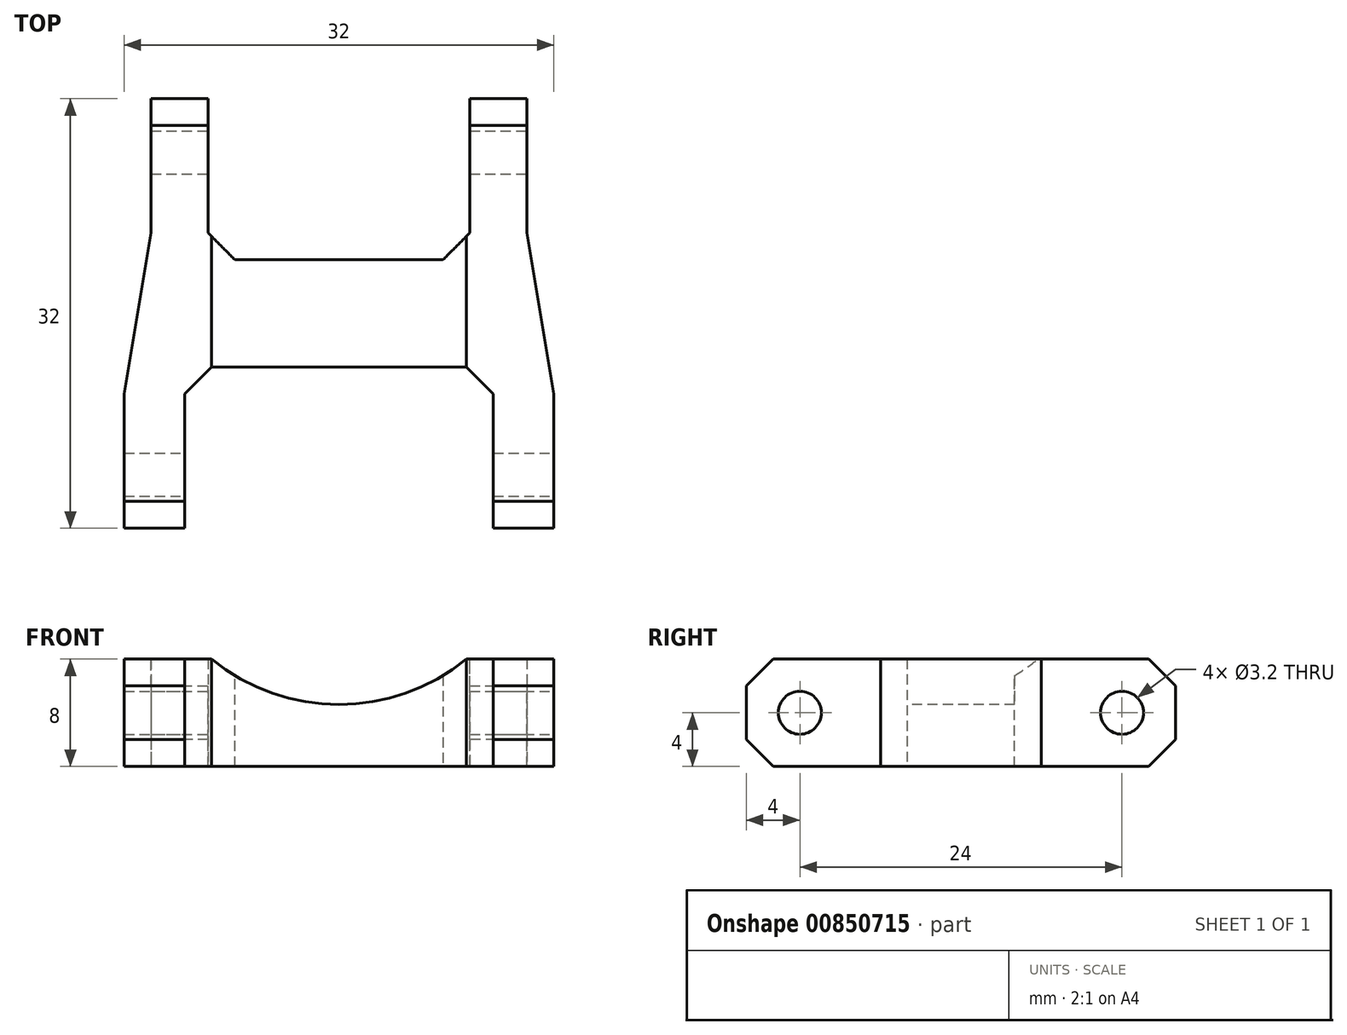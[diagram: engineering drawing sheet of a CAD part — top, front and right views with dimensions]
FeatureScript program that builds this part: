
annotation { "Feature Type Name" : "Feature", "Feature Type Description" : "" }
export const myFeature = defineFeature(function(context is Context, id is Id, definition is map)
    precondition{}
    {
        {
            var Q0;
            Q0=qCreatedBy(makeId("Top.planeOp"),FACE);
            var sketch = newSketch(context, id + "F0", { "sketchPlane" : qUnion([Q0])});
            skLineSegment(sketch, "E0", {"start": v(-14, 22) * mm, "end": v(14, 22) * mm});
            skLineSegment(sketch, "E1", {"start": v(14, 22) * mm, "end": v(14, 12) * mm});
            skLineSegment(sketch, "E2", {"start": v(14, 12) * mm, "end": v(16, 0) * mm});
            skLineSegment(sketch, "E3", {"start": v(16, 0) * mm, "end": v(16, -10) * mm});
            skLineSegment(sketch, "E4", {"start": v(16, -10) * mm, "end": v(-16, -10) * mm});
            skLineSegment(sketch, "E5", {"start": v(-14, 12) * mm, "end": v(-14, 22) * mm});
            skLineSegment(sketch, "E6", {"start": v(-16, -10) * mm, "end": v(-16, 0) * mm});
            skLineSegment(sketch, "E7", {"start": v(-16, 0) * mm, "end": v(-14, 12) * mm});
            skSolve(sketch);
        }
        {
            var Q0;
            Q0=qSketchRegion(id+"F0",true);
            extrude(context, id + "F1", {"entities" : qUnion([Q0]), "depth" : 8 * mm, "offsetDistance" : 25 * mm});
        }
        {
            var Q0;
            Q0=makeQuery(id+"F1.opExtrude","CAP_FACE",FACE,{"disambiguationData":[OSD([sQuery(id+"F0.wireOp",EDGE,"E0"),sQuery(id+"F0.wireOp",EDGE,"E1"),sQuery(id+"F0.wireOp",EDGE,"E2"),sQuery(id+"F0.wireOp",EDGE,"E3"),sQuery(id+"F0.wireOp",EDGE,"E4"),sQuery(id+"F0.wireOp",EDGE,"E5"),sQuery(id+"F0.wireOp",EDGE,"E6"),sQuery(id+"F0.wireOp",EDGE,"E7")])],"isStart":false});
            var sketch = newSketch(context, id + "F2", { "sketchPlane" : qUnion([Q0])});
            skLineSegment(sketch, "E8.bottom", {"start": v(-9.75, 22) * mm, "end": v(9.75, 22) * mm});
            skLineSegment(sketch, "E8.top", {"start": v(-9.75, 10) * mm, "end": v(9.75, 10) * mm});
            skLineSegment(sketch, "E8.left", {"start": v(-9.75, 22) * mm, "end": v(-9.75, 10) * mm});
            skLineSegment(sketch, "E8.right", {"start": v(9.75, 22) * mm, "end": v(9.75, 10) * mm});
            skLineSegment(sketch, "E9.bottom", {"start": v(-11.5, -10) * mm, "end": v(11.5, -10) * mm});
            skLineSegment(sketch, "E9.top", {"start": v(-11.5, 2) * mm, "end": v(11.5, 2) * mm});
            skLineSegment(sketch, "E9.left", {"start": v(-11.5, -10) * mm, "end": v(-11.5, 2) * mm});
            skLineSegment(sketch, "E9.right", {"start": v(11.5, -10) * mm, "end": v(11.5, 2) * mm});
            skSolve(sketch);
        }
        {
            var Q0;
            Q0=qSketchRegion(id+"F2",true);
            extrude(context, id + "F3", {"entities" : qUnion([Q0]), "operationType" : NewBodyOperationType.REMOVE, "endBound" : BoundingType.UP_TO_NEXT, "oppositeDirection" : true, "depth" : 25 * mm, "offsetDistance" : 25 * mm});
        }
        {
            var Q0;
            Q0=makeQuery(id+"F1.opExtrude","SWEPT_FACE",FACE,{"disambiguationData":[OSD([sQuery(id+"F0.wireOp",EDGE,"E3")])]});
            var sketch = newSketch(context, id + "F4", { "sketchPlane" : qUnion([Q0])});
            skCircle(sketch, "E10", {"center": v(-6, 4) * mm, "radius": 1.6 * mm});
            skLineSegment(sketch, "E11", {"start": v(-10, 0) * mm, "end": v(-2, 8) * mm, "construction": true});
            skLineSegment(sketch, "E12", {"start": v(-2, 8) * mm, "end": v(-10, 8) * mm, "construction": true});
            skSolve(sketch);
        }
        {
            var Q0;
            Q0=qSketchRegion(id+"F4",true);
            var Q1;
            Q1=makeQuery(id+"F1.opExtrude","SWEPT_FACE",FACE,{"disambiguationData":[OSD([sQuery(id+"F0.wireOp",EDGE,"E6")])]});
            extrude(context, id + "F5", {"entities" : qUnion([Q0]), "operationType" : NewBodyOperationType.REMOVE, "endBound" : BoundingType.UP_TO_SURFACE, "oppositeDirection" : true, "depth" : 25 * mm, "endBoundEntityFace" : qUnion([Q1]), "offsetDistance" : 25 * mm});
        }
        {
            var Q0;
            Q0=makeQuery(id+"F1.opExtrude","SWEPT_FACE",FACE,{"disambiguationData":[OSD([sQuery(id+"F0.wireOp",EDGE,"E1")])]});
            var sketch = newSketch(context, id + "F6", { "sketchPlane" : qUnion([Q0])});
            skCircle(sketch, "E13", {"center": v(18, 4) * mm, "radius": 1.6 * mm});
            skLineSegment(sketch, "E14", {"start": v(22, 8) * mm, "end": v(14, 0) * mm, "construction": true});
            skLineSegment(sketch, "E15", {"start": v(14, 0) * mm, "end": v(22, 0) * mm, "construction": true});
            skSolve(sketch);
        }
        {
            var Q0;
            Q0=qSketchRegion(id+"F6",true);
            var Q1;
            Q1=makeQuery(id+"F1.opExtrude","SWEPT_FACE",FACE,{"disambiguationData":[OSD([sQuery(id+"F0.wireOp",EDGE,"E5")])]});
            extrude(context, id + "F7", {"entities" : qUnion([Q0]), "operationType" : NewBodyOperationType.REMOVE, "endBound" : BoundingType.UP_TO_SURFACE, "oppositeDirection" : true, "depth" : 25 * mm, "endBoundEntityFace" : qUnion([Q1]), "offsetDistance" : 25 * mm});
        }
        {
            var Q0;
            Q0=makeQuery(id+"F3.boolean.opBoolean","COPY",EDGE,{"derivedFrom":makeQuery(id+"F3.opExtrude","SWEPT_EDGE",EDGE,{"disambiguationData":[OSD([sQuery(id+"F2.wireOp",EDGE,"E8.top"),sQuery(id+"F2.wireOp",EDGE,"E8.right")])]})});
            var Q1;
            Q1=makeQuery(id+"F3.boolean.opBoolean","COPY",EDGE,{"derivedFrom":makeQuery(id+"F3.opExtrude","SWEPT_EDGE",EDGE,{"disambiguationData":[OSD([sQuery(id+"F2.wireOp",EDGE,"E8.top"),sQuery(id+"F2.wireOp",EDGE,"E8.left")])]})});
            var Q2;
            Q2=makeQuery(id+"F3.boolean.opBoolean","COPY",EDGE,{"derivedFrom":makeQuery(id+"F3.opExtrude","SWEPT_EDGE",EDGE,{"disambiguationData":[OSD([sQuery(id+"F2.wireOp",EDGE,"E9.top"),sQuery(id+"F2.wireOp",EDGE,"E9.right")])]})});
            var Q3;
            Q3=makeQuery(id+"F3.boolean.opBoolean","COPY",EDGE,{"derivedFrom":makeQuery(id+"F3.opExtrude","SWEPT_EDGE",EDGE,{"disambiguationData":[OSD([sQuery(id+"F2.wireOp",EDGE,"E9.top"),sQuery(id+"F2.wireOp",EDGE,"E9.left")])]})});
            chamfer(context, id + "F8", {"entities" : qUnion([Q0, Q1, Q2, Q3]), "width" : 2 * mm, "tangentPropagation" : true});
        }
        {
            var Q0;
            Q0=makeQuery(id+"F3.boolean.opBoolean","COPY",FACE,{"derivedFrom":makeQuery(id+"F3.opExtrude","SWEPT_FACE",FACE,{"disambiguationData":[OSD([sQuery(id+"F2.wireOp",EDGE,"E9.top")])]})});
            var sketch = newSketch(context, id + "F9", { "sketchPlane" : qUnion([Q0])});
            skArc(sketch, "E16", {"start": v(-9.5, 8) * mm, "mid": v(0, 4.6) * mm, "end": v(9.5, 8) * mm});
            skLineSegment(sketch, "E17", {"start": v(-9.5, 8) * mm, "end": v(9.5, 8) * mm});
            skSolve(sketch);
        }
        {
            var Q0;
            Q0 = qSketchRegion(id + "F9", true);
            extrude(context, id + "F10", {"entities" : qUnion([Q0]), "operationType" : NewBodyOperationType.REMOVE, "endBound" : BoundingType.UP_TO_NEXT, "oppositeDirection" : true, "depth" : 25 * mm, "offsetDistance" : 25 * mm});
        }
        {
            var Q0;
            {var subQ0=sQuery(id+"F0.wireOp",EDGE,"E6");var subQ1=sQuery(id+"F0.wireOp",EDGE,"E4");Q0=makeQuery(id+"F3.boolean.opBoolean","SPLIT",EDGE,{"disambiguationData":[TD([makeQuery(id+"F1.opExtrude","SWEPT_FACE",FACE,{"disambiguationData":[OSD([subQ0])]})])],"derivedFrom":makeQuery(id+"F1.opExtrude","CAP_EDGE",EDGE,{"disambiguationData":[OSD([subQ1])],"isStart":false})});}
            var Q1;
            {var subQ0=sQuery(id+"F0.wireOp",EDGE,"E6");var subQ1=sQuery(id+"F0.wireOp",EDGE,"E4");Q1=makeQuery(id+"F3.boolean.opBoolean","SPLIT",EDGE,{"disambiguationData":[TD([makeQuery(id+"F1.opExtrude","SWEPT_FACE",FACE,{"disambiguationData":[OSD([subQ0])]})])],"derivedFrom":makeQuery(id+"F1.opExtrude","CAP_EDGE",EDGE,{"disambiguationData":[OSD([subQ1])],"isStart":true})});}
            var Q2;
            {var subQ0=sQuery(id+"F0.wireOp",EDGE,"E4");var subQ1=sQuery(id+"F0.wireOp",EDGE,"E3");Q2=makeQuery(id+"F3.boolean.opBoolean","SPLIT",EDGE,{"disambiguationData":[TD([makeQuery(id+"F1.opExtrude","SWEPT_FACE",FACE,{"disambiguationData":[OSD([subQ1])]})])],"derivedFrom":makeQuery(id+"F1.opExtrude","CAP_EDGE",EDGE,{"disambiguationData":[OSD([subQ0])],"isStart":false})});}
            var Q3;
            {var subQ0=sQuery(id+"F0.wireOp",EDGE,"E4");var subQ1=sQuery(id+"F0.wireOp",EDGE,"E3");Q3=makeQuery(id+"F3.boolean.opBoolean","SPLIT",EDGE,{"disambiguationData":[TD([makeQuery(id+"F1.opExtrude","SWEPT_FACE",FACE,{"disambiguationData":[OSD([subQ1])]})])],"derivedFrom":makeQuery(id+"F1.opExtrude","CAP_EDGE",EDGE,{"disambiguationData":[OSD([subQ0])],"isStart":true})});}
            var Q4;
            {var subQ0=sQuery(id+"F0.wireOp",EDGE,"E0");var subQ1=sQuery(id+"F0.wireOp",EDGE,"E1");Q4=makeQuery(id+"F3.boolean.opBoolean","SPLIT",EDGE,{"disambiguationData":[TD([makeQuery(id+"F1.opExtrude","SWEPT_FACE",FACE,{"disambiguationData":[OSD([subQ1])]})])],"derivedFrom":makeQuery(id+"F1.opExtrude","CAP_EDGE",EDGE,{"disambiguationData":[OSD([subQ0])],"isStart":false})});}
            var Q5;
            {var subQ0=sQuery(id+"F0.wireOp",EDGE,"E0");var subQ1=sQuery(id+"F0.wireOp",EDGE,"E1");Q5=makeQuery(id+"F3.boolean.opBoolean","SPLIT",EDGE,{"disambiguationData":[TD([makeQuery(id+"F1.opExtrude","SWEPT_FACE",FACE,{"disambiguationData":[OSD([subQ1])]})])],"derivedFrom":makeQuery(id+"F1.opExtrude","CAP_EDGE",EDGE,{"disambiguationData":[OSD([subQ0])],"isStart":true})});}
            var Q6;
            {var subQ0=sQuery(id+"F0.wireOp",EDGE,"E0");var subQ1=sQuery(id+"F0.wireOp",EDGE,"E5");Q6=makeQuery(id+"F3.boolean.opBoolean","SPLIT",EDGE,{"disambiguationData":[TD([makeQuery(id+"F1.opExtrude","SWEPT_FACE",FACE,{"disambiguationData":[OSD([subQ1])]})])],"derivedFrom":makeQuery(id+"F1.opExtrude","CAP_EDGE",EDGE,{"disambiguationData":[OSD([subQ0])],"isStart":true})});}
            var Q7;
            {var subQ0=sQuery(id+"F0.wireOp",EDGE,"E0");var subQ1=sQuery(id+"F0.wireOp",EDGE,"E5");Q7=makeQuery(id+"F3.boolean.opBoolean","SPLIT",EDGE,{"disambiguationData":[TD([makeQuery(id+"F1.opExtrude","SWEPT_FACE",FACE,{"disambiguationData":[OSD([subQ1])]})])],"derivedFrom":makeQuery(id+"F1.opExtrude","CAP_EDGE",EDGE,{"disambiguationData":[OSD([subQ0])],"isStart":false})});}
            var Q8;
            Q8=makeQuery(id+"F3.boolean.opBoolean","COPY",EDGE,{"derivedFrom":makeQuery(id+"F3.opExtrude","TWEAK_EDGE",EDGE,{"derivedFrom":[makeQuery(id+"F1.opExtrude","CAP_FACE",FACE,{"disambiguationData":[OSD([sQuery(id+"F0.wireOp",EDGE,"E0"),sQuery(id+"F0.wireOp",EDGE,"E1"),sQuery(id+"F0.wireOp",EDGE,"E2"),sQuery(id+"F0.wireOp",EDGE,"E3"),sQuery(id+"F0.wireOp",EDGE,"E4"),sQuery(id+"F0.wireOp",EDGE,"E5"),sQuery(id+"F0.wireOp",EDGE,"E6"),sQuery(id+"F0.wireOp",EDGE,"E7")])],"isStart":true}),makeQuery(id+"F2.imprint","IMPRINT",EDGE,{"derivedFrom":sQuery(id+"F2.wireOp",EDGE,"E8.top")})]})});
            var Q9;
            Q9=makeQuery(id+"F3.boolean.opBoolean","COPY",EDGE,{"derivedFrom":makeQuery(id+"F3.opExtrude","TWEAK_EDGE",EDGE,{"derivedFrom":[makeQuery(id+"F1.opExtrude","CAP_FACE",FACE,{"disambiguationData":[OSD([sQuery(id+"F0.wireOp",EDGE,"E0"),sQuery(id+"F0.wireOp",EDGE,"E1"),sQuery(id+"F0.wireOp",EDGE,"E2"),sQuery(id+"F0.wireOp",EDGE,"E3"),sQuery(id+"F0.wireOp",EDGE,"E4"),sQuery(id+"F0.wireOp",EDGE,"E5"),sQuery(id+"F0.wireOp",EDGE,"E6"),sQuery(id+"F0.wireOp",EDGE,"E7")])],"isStart":true}),makeQuery(id+"F2.imprint","IMPRINT",EDGE,{"derivedFrom":sQuery(id+"F2.wireOp",EDGE,"E9.top")})]})});
            var Q10;
            Q10=makeQuery(id+"F10.boolean.opBoolean","COPY",EDGE,{"derivedFrom":makeQuery(id+"F10.opExtrude","CAP_EDGE",EDGE,{"disambiguationData":[OSD([sQuery(id+"F9.wireOp",EDGE,"E16")])],"isStart":true})});
            var Q11;
            Q11=makeQuery(id+"F10.boolean.opBoolean","COPY",EDGE,{"derivedFrom":makeQuery(id+"F10.opExtrude","TWEAK_EDGE",EDGE,{"derivedFrom":[makeQuery(id+"F3.boolean.opBoolean","COPY",FACE,{"derivedFrom":makeQuery(id+"F3.opExtrude","SWEPT_FACE",FACE,{"disambiguationData":[OSD([sQuery(id+"F2.wireOp",EDGE,"E8.top")])]})}),makeQuery(id+"F9.imprint","IMPRINT",EDGE,{"derivedFrom":sQuery(id+"F9.wireOp",EDGE,"E16")})]})});
            chamfer(context, id + "F11", {"entities" : qUnion([Q0, Q1, Q2, Q3, Q4, Q5, Q6, Q7, Q8, Q9, Q10, Q11]), "width" : 2 * mm, "tangentPropagation" : true});
        }
    });
